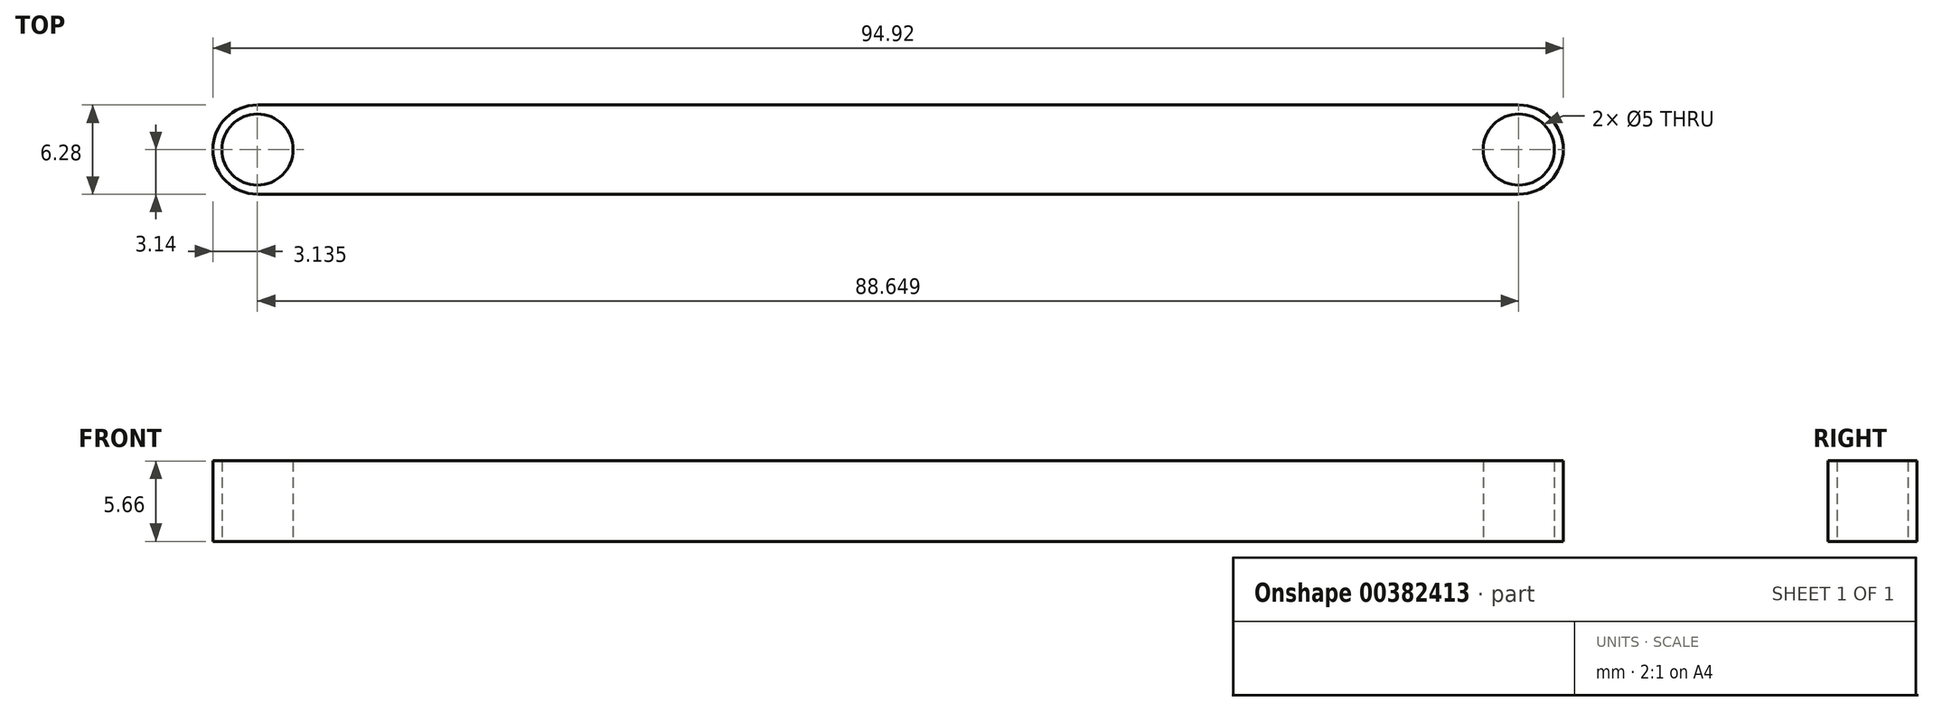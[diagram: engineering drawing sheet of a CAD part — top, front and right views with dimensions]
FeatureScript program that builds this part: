
annotation { "Feature Type Name" : "Feature", "Feature Type Description" : "" }
export const myFeature = defineFeature(function(context is Context, id is Id, definition is map)
    precondition{}
    {
        {
            var Q0;
            Q0=qCreatedBy(makeId("Top.planeOp"),FACE);
            var sketch = newSketch(context, id + "F0", { "sketchPlane" : qUnion([Q0])});
            skLineSegment(sketch, "E0.bottom", {"start": v(-44.32, 3.14) * mm, "end": v(44.32, 3.14) * mm});
            skLineSegment(sketch, "E0.top", {"start": v(-44.32, -3.14) * mm, "end": v(44.32, -3.14) * mm});
            skLineSegment(sketch, "E0.left", {"start": v(-44.32, 3.14) * mm, "end": v(-44.32, -3.14) * mm});
            skLineSegment(sketch, "E0.right", {"start": v(44.32, 3.14) * mm, "end": v(44.32, -3.14) * mm});
            skPoint(sketch, "E0.middle", {"position": v(0, 0) * mm});
            skCircle(sketch, "E1", {"center": v(-44.32, 0) * mm, "radius": 3.14 * mm});
            skCircle(sketch, "E2", {"center": v(44.32, 0) * mm, "radius": 3.14 * mm});
            skCircle(sketch, "E3", {"center": v(-44.32, 0) * mm, "radius": 2.5 * mm});
            skCircle(sketch, "E4", {"center": v(44.32, 0) * mm, "radius": 2.5 * mm});
            skSolve(sketch);
        }
        {
            var Q0;
            {var subQ1=sQuery(id+"F0.wireOp",EDGE,"E0.left");var subQ3=sQuery(id+"F0.wireOp",EDGE,"E3");var subQ4=makeQuery(id+"F0.imprint","INTERSECT",VERTEX,{"disambiguationData":[OD(0.0)],"derivedFrom":[subQ1,subQ3]});Q0=makeQuery(id+"F0.imprint","IMPRINT",FACE,{"disambiguationData":[TD([[makeQuery(id+"F0.imprint","IMPRINT",EDGE,{"disambiguationData":[TD([[subQ4,1.0]])],"derivedFrom":subQ3}),-1.0]])]});}
            var Q1;
            {var subQ1=sQuery(id+"F0.wireOp",EDGE,"E0.left");var subQ3=sQuery(id+"F0.wireOp",EDGE,"E3");var subQ4=makeQuery(id+"F0.imprint","INTERSECT",VERTEX,{"disambiguationData":[OD(0.0)],"derivedFrom":[subQ1,subQ3]});Q1=makeQuery(id+"F0.imprint","IMPRINT",FACE,{"disambiguationData":[TD([[makeQuery(id+"F0.imprint","IMPRINT",EDGE,{"disambiguationData":[TD([[subQ4,-1.0]])],"derivedFrom":subQ3}),-1.0]])]});}
            var Q2;
            {var subQ0=sQuery(id+"F0.wireOp",EDGE,"E0.bottom");Q2=makeQuery(id+"F0.imprint","IMPRINT",FACE,{"disambiguationData":[TD([[makeQuery(id+"F0.imprint","IMPRINT",EDGE,{"derivedFrom":subQ0}),-1.0]])]});}
            var Q3;
            {var subQ1=sQuery(id+"F0.wireOp",EDGE,"E0.right");var subQ3=sQuery(id+"F0.wireOp",EDGE,"E4");var subQ4=makeQuery(id+"F0.imprint","INTERSECT",VERTEX,{"disambiguationData":[OD(0.0)],"derivedFrom":[subQ1,subQ3]});Q3=makeQuery(id+"F0.imprint","IMPRINT",FACE,{"disambiguationData":[TD([[makeQuery(id+"F0.imprint","IMPRINT",EDGE,{"disambiguationData":[TD([[subQ4,-1.0]])],"derivedFrom":subQ3}),-1.0]])]});}
            var Q4;
            {var subQ1=sQuery(id+"F0.wireOp",EDGE,"E0.right");var subQ3=sQuery(id+"F0.wireOp",EDGE,"E4");var subQ4=makeQuery(id+"F0.imprint","INTERSECT",VERTEX,{"disambiguationData":[OD(0.0)],"derivedFrom":[subQ1,subQ3]});Q4=makeQuery(id+"F0.imprint","IMPRINT",FACE,{"disambiguationData":[TD([[makeQuery(id+"F0.imprint","IMPRINT",EDGE,{"disambiguationData":[TD([[subQ4,1.0]])],"derivedFrom":subQ3}),-1.0]])]});}
            extrude(context, id + "F1", {"entities" : qUnion([Q0, Q1, Q2, Q3, Q4]), "depth" : 5.66 * mm});
        }
    });
